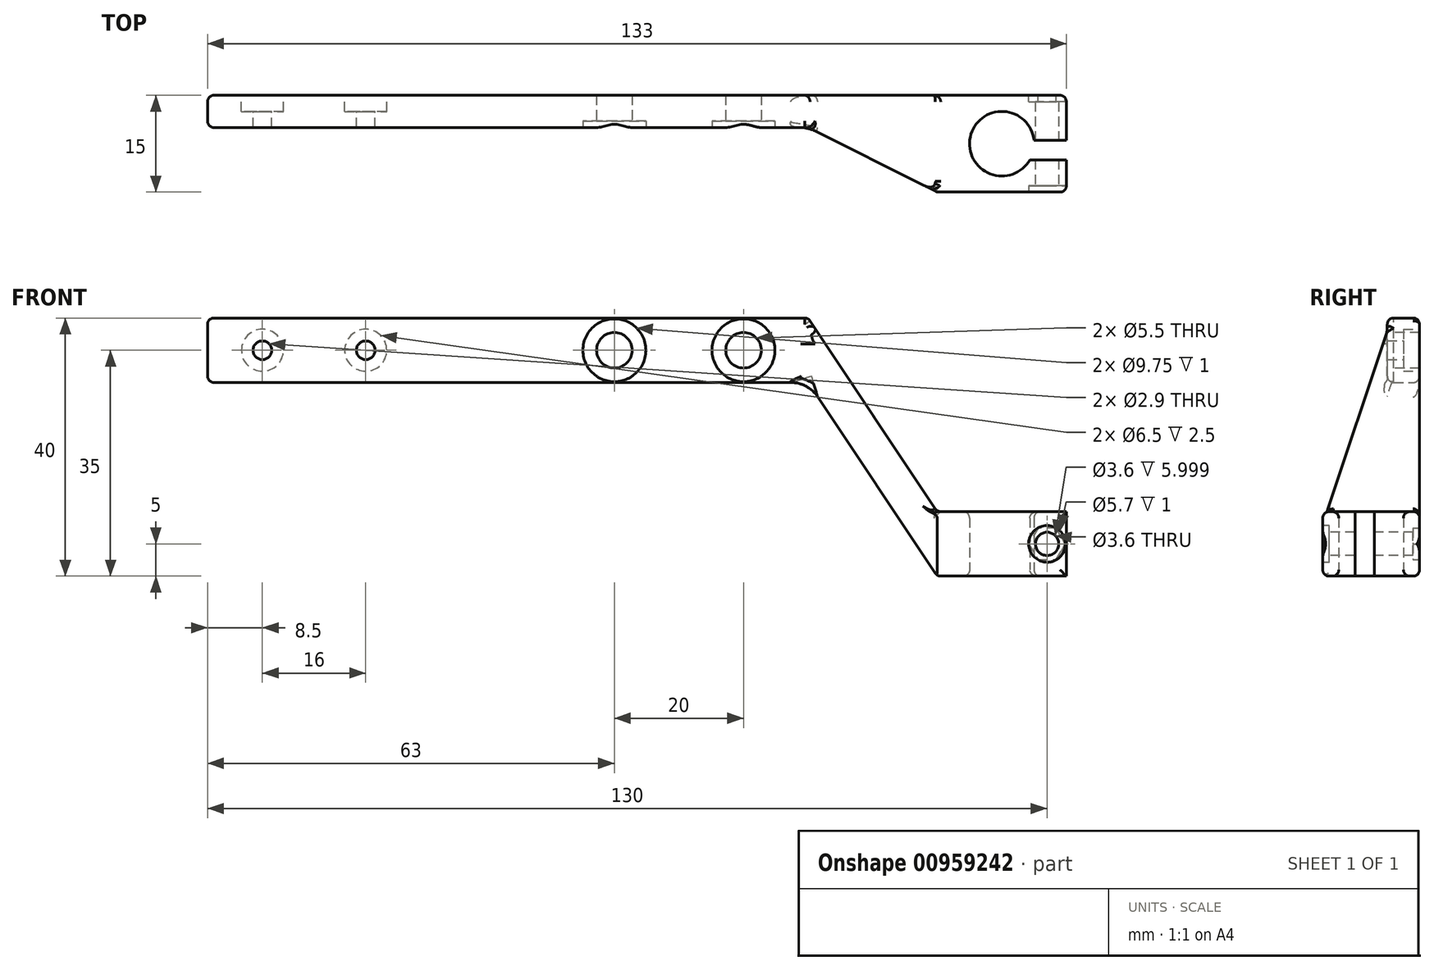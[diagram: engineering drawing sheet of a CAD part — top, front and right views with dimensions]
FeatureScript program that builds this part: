
annotation { "Feature Type Name" : "Feature", "Feature Type Description" : "" }
export const myFeature = defineFeature(function(context is Context, id is Id, definition is map)
    precondition{}
    {
        {
            var Q0;
            Q0=qCreatedBy(makeId("Top.planeOp"),FACE);
            var sketch = newSketch(context, id + "F0", { "sketchPlane" : qUnion([Q0])});
            skLineSegment(sketch, "E0.bottom", {"start": v(0, 0) * mm, "end": v(40, 0) * mm});
            skLineSegment(sketch, "E0.top", {"start": v(0, -5) * mm, "end": v(40, -5) * mm});
            skLineSegment(sketch, "E0.left", {"start": v(0, 0) * mm, "end": v(0, -5) * mm});
            skLineSegment(sketch, "E0.right", {"start": v(40, 0) * mm, "end": v(40, -5) * mm});
            skLineSegment(sketch, "E1.MirrorCS", {"start": v(80, 0) * mm, "end": v(40, 0) * mm});
            skLineSegment(sketch, "E2.MirrorCS", {"start": v(80, -5) * mm, "end": v(40, -5) * mm});
            skLineSegment(sketch, "E3.MirrorCS", {"start": v(80, 0) * mm, "end": v(80, -5) * mm});
            skPoint(sketch, "E4.oppositeSnap0", {"position": v(60, 0) * mm});
            skLineSegment(sketch, "E4.bottom", {"start": v(80, 0) * mm, "end": v(60, 0) * mm});
            skLineSegment(sketch, "E4.top", {"start": v(80, 5) * mm, "end": v(60, 5) * mm});
            skLineSegment(sketch, "E4.left", {"start": v(80, 0) * mm, "end": v(80, 5) * mm});
            skLineSegment(sketch, "E4.right", {"start": v(60, 0) * mm, "end": v(60, 5) * mm});
            skPoint(sketch, "E5.oppositeSnap0", {"position": v(60, -5) * mm});
            skLineSegment(sketch, "E5.bottom", {"start": v(80, -5) * mm, "end": v(60, -5) * mm});
            skLineSegment(sketch, "E5.top", {"start": v(80, -10) * mm, "end": v(60, -10) * mm});
            skLineSegment(sketch, "E5.left", {"start": v(80, -5) * mm, "end": v(80, -10) * mm});
            skLineSegment(sketch, "E5.right", {"start": v(60, -5) * mm, "end": v(60, -10) * mm});
            skLineSegment(sketch, "E6", {"start": v(40, -5) * mm, "end": v(60, -10) * mm});
            skLineSegment(sketch, "E7", {"start": v(40, 0) * mm, "end": v(60, 5) * mm});
            skPoint(sketch, "E8", {"position": v(70, -2.5) * mm});
            skPoint(sketch, "E8.positionSnap0", {"position": v(70, 0) * mm});
            skLineSegment(sketch, "E9", {"start": v(70, 0) * mm, "end": v(70, -5) * mm, "construction": true});
            skCircle(sketch, "E10", {"center": v(70, -2.5) * mm, "radius": 5 * mm});
            skLineSegment(sketch, "E11.bottom", {"start": v(80, -3) * mm, "end": v(74.97, -3) * mm});
            skLineSegment(sketch, "E11.top", {"start": v(80, -3) * mm, "end": v(74.97, -3) * mm});
            skLineSegment(sketch, "E11.left", {"start": v(80, -3) * mm, "end": v(80, -3) * mm});
            skLineSegment(sketch, "E11.right", {"start": v(74.97, -3) * mm, "end": v(74.97, -3) * mm});
            skLineSegment(sketch, "E12", {"start": v(70, -2.5) * mm, "end": v(80, -2.5) * mm, "construction": true});
            skLineSegment(sketch, "E13.MirrorCS", {"start": v(80, -2) * mm, "end": v(74.97, -2) * mm});
            skLineSegment(sketch, "E14", {"start": v(60, 0) * mm, "end": v(60, -5) * mm});
            skSolve(sketch);
        }
        {
            var Q0;
            Q0=makeQuery(id+"F0.imprint","IMPRINT",FACE,{"disambiguationData":[TD([[makeQuery(id+"F0.imprint","IMPRINT",EDGE,{"derivedFrom":sQuery(id+"F0.wireOp",EDGE,"E0.bottom")}),-1.0]])]});
            extrude(context, id + "F1", {"entities" : qUnion([Q0]), "depth" : 10 * mm, "offsetDistance" : 25 * mm});
        }
        {
            var Q0;
            Q0=makeQuery(id+"F0.imprint","IMPRINT",FACE,{"disambiguationData":[TD([[makeQuery(id+"F0.imprint","IMPRINT",EDGE,{"derivedFrom":sQuery(id+"F0.wireOp",EDGE,"E5.top")}),-1.0]])]});
            var Q1;
            {var subQ0=sQuery(id+"F0.wireOp",EDGE,"E14");Q1=makeQuery(id+"F0.imprint","IMPRINT",FACE,{"disambiguationData":[TD([[makeQuery(id+"F0.imprint","IMPRINT",EDGE,{"derivedFrom":subQ0}),1.0]])]});}
            var Q2;
            Q2=makeQuery(id+"F0.imprint","IMPRINT",FACE,{"disambiguationData":[TD([[makeQuery(id+"F0.imprint","IMPRINT",EDGE,{"derivedFrom":sQuery(id+"F0.wireOp",EDGE,"E4.top")}),1.0]])]});
            var Q3;
            {var subQ3=sQuery(id+"F0.wireOp",EDGE,"E13.MirrorCS");Q3=makeQuery(id+"F0.imprint","IMPRINT",FACE,{"disambiguationData":[TD([[makeQuery(id+"F0.imprint","IMPRINT",EDGE,{"derivedFrom":subQ3}),-1.0]])]});}
            var Q4;
            {var subQ3=sQuery(id+"F0.wireOp",EDGE,"E11.top");Q4=makeQuery(id+"F0.imprint","IMPRINT",FACE,{"disambiguationData":[TD([[makeQuery(id+"F0.imprint","IMPRINT",EDGE,{"derivedFrom":subQ3}),1.0]])]});}
            extrude(context, id + "F2", {"entities" : qUnion([Q0, Q1, Q2, Q3, Q4]), "operationType" : NewBodyOperationType.ADD, "depth" : 10 * mm, "offsetDistance" : 25 * mm});
        }
        {
            var Q0;
            Q0=makeQuery(id+"F1.opExtrude","SWEPT_FACE",FACE,{"disambiguationData":[OSD([sQuery(id+"F0.wireOp",EDGE,"E0.top")])]});
            var sketch = newSketch(context, id + "F3", { "sketchPlane" : qUnion([Q0])});
            skLineSegment(sketch, "E15", {"start": v(0, 5) * mm, "end": v(10, 5) * mm, "construction": true});
            skLineSegment(sketch, "E16", {"start": v(10, 5) * mm, "end": v(30, 5) * mm, "construction": true});
            skLineSegment(sketch, "E17", {"start": v(30, 5) * mm, "end": v(40, 5) * mm, "construction": true});
            skSolve(sketch);
        }
        {
            var Q0;
            Q0=makeQuery(id+"F2.opExtrude","SWEPT_FACE",FACE,{"disambiguationData":[OSD([sQuery(id+"F0.wireOp",EDGE,"E5.top")])]});
            var sketch = newSketch(context, id + "F4", { "sketchPlane" : qUnion([Q0])});
            skLineSegment(sketch, "E18", {"start": v(80, 5) * mm, "end": v(77, 5) * mm, "construction": true});
            skLineSegment(sketch, "E19", {"start": v(77, 5) * mm, "end": v(60, 5) * mm, "construction": true});
            skSolve(sketch);
        }
        {
            var Q0;
            Q0=sQuery(id+"F3.wireOp",VERTEX,"E15.end");
            var Q1;
            Q1=sQuery(id+"F3.wireOp",VERTEX,"E16.end");
            var Q2;
            Q2=makeQuery(id+"F1.opExtrude","SWEPT_BODY",BODY,{"disambiguationData":[OSD([sQuery(id+"F0.wireOp",EDGE,"E0.bottom"),sQuery(id+"F0.wireOp",EDGE,"E0.top"),sQuery(id+"F0.wireOp",EDGE,"E0.left"),sQuery(id+"F0.wireOp",EDGE,"E3.MirrorCS"),sQuery(id+"F0.wireOp",EDGE,"E4.top"),sQuery(id+"F0.wireOp",EDGE,"E4.left"),sQuery(id+"F0.wireOp",EDGE,"E5.top"),sQuery(id+"F0.wireOp",EDGE,"E5.left"),sQuery(id+"F0.wireOp",EDGE,"E6"),sQuery(id+"F0.wireOp",EDGE,"E7"),sQuery(id+"F0.wireOp",EDGE,"E10"),sQuery(id+"F0.wireOp",EDGE,"E11.top"),sQuery(id+"F0.wireOp",EDGE,"E13.MirrorCS")])]});
            hole(context, id + "F5", {"style" : HoleStyle.C_BORE, "endStyle" : HoleEndStyle.THROUGH, "holeDiameter" : 5.5 * mm, "cBoreDiameter" : 9.75 * mm, "cBoreDepth" : 1 * mm, "majorDiameter" : 5 * mm, "isTappedThrough" : true, "tappedDepth" : 12 * mm, "tapClearance" : 3, "locations" : qUnion([Q0, Q1]), "scope" : qUnion([Q2])});
        }
        {
            var Q0;
            Q0=sQuery(id+"F4.wireOp",VERTEX,"E18.end");
            var Q1;
            Q1=makeQuery(id+"F2.opExtrude","SWEPT_BODY",BODY,{"disambiguationData":[OSD([sQuery(id+"F0.wireOp",EDGE,"E3.MirrorCS"),sQuery(id+"F0.wireOp",EDGE,"E4.top"),sQuery(id+"F0.wireOp",EDGE,"E4.left"),sQuery(id+"F0.wireOp",EDGE,"E4.right"),sQuery(id+"F0.wireOp",EDGE,"E5.top"),sQuery(id+"F0.wireOp",EDGE,"E5.left"),sQuery(id+"F0.wireOp",EDGE,"E5.right"),sQuery(id+"F0.wireOp",EDGE,"E10"),sQuery(id+"F0.wireOp",EDGE,"E11.top"),sQuery(id+"F0.wireOp",EDGE,"E13.MirrorCS"),sQuery(id+"F0.wireOp",EDGE,"E14")])]});
            hole(context, id + "F6", {"style" : HoleStyle.C_BORE, "endStyle" : HoleEndStyle.THROUGH, "holeDiameter" : 3.6 * mm, "cBoreDiameter" : 5.7 * mm, "cBoreDepth" : 1 * mm, "majorDiameter" : 5 * mm, "isTappedThrough" : true, "tappedDepth" : 12 * mm, "tapClearance" : 3, "locations" : qUnion([Q0]), "scope" : qUnion([Q1])});
        }
        {
            var Q0;
            Q0=makeQuery(id+"F2.opExtrude","SWEPT_FACE",FACE,{"disambiguationData":[OSD([sQuery(id+"F0.wireOp",EDGE,"E4.top")])]});
            var sketch = newSketch(context, id + "F7", { "sketchPlane" : qUnion([Q0])});
            skCircle(sketch, "E20.cCircle", {"center": v(-77, 5) * mm, "radius": 2.45 * mm, "construction": true});
            skLineSegment(sketch, "E20.0", {"start": v(-75.58, 2.55) * mm, "end": v(-78.42, 2.55) * mm});
            skLineSegment(sketch, "E20.1", {"start": v(-78.42, 2.55) * mm, "end": v(-79.83, 5) * mm});
            skLineSegment(sketch, "E20.2", {"start": v(-79.83, 5) * mm, "end": v(-78.42, 7.45) * mm});
            skLineSegment(sketch, "E20.3", {"start": v(-78.42, 7.45) * mm, "end": v(-75.58, 7.45) * mm});
            skLineSegment(sketch, "E20.4", {"start": v(-75.58, 7.45) * mm, "end": v(-74.17, 5) * mm});
            skLineSegment(sketch, "E20.5", {"start": v(-74.17, 5) * mm, "end": v(-75.58, 2.55) * mm});
            skPoint(sketch, "E20.0.midPoint", {"position": v(-77, 2.55) * mm});
            skSolve(sketch);
        }
        {
            var Q0;
            Q0=makeQuery(id+"F7.imprint","IMPRINT",FACE,{"disambiguationData":[TD([[makeQuery(id+"F7.imprint","IMPRINT",EDGE,{"derivedFrom":makeQuery(id+"F6.hole-0.boolean.opBoolean","INTERSECT",EDGE,{"derivedFrom":[makeQuery(id+"F2.opExtrude","SWEPT_FACE",FACE,{"disambiguationData":[OSD([sQuery(id+"F0.wireOp",EDGE,"E4.top")])]}),makeQuery(id+"F6.hole-0.opRevolve","SWEPT_FACE",FACE,{"disambiguationData":[OSD([sQuery(id+"F6.hole-0.sketch.wireOp",EDGE,"core_line_2")])]})]})}),1.0]])]});
            var Q1;
            Q1=makeQuery(id+"F7.imprint","IMPRINT",FACE,{"disambiguationData":[TD([[makeQuery(id+"F7.imprint","IMPRINT",EDGE,{"derivedFrom":sQuery(id+"F7.wireOp",EDGE,"E20.0")}),-1.0]])]});
            extrude(context, id + "F8", {"entities" : qUnion([Q0, Q1]), "operationType" : NewBodyOperationType.REMOVE, "oppositeDirection" : true, "depth" : 1 * mm, "offsetDistance" : 25 * mm});
        }
        {
            var Q0;
            Q0=makeQuery(id+"F2.opExtrude","SWEPT_BODY",BODY,{"disambiguationData":[OSD([sQuery(id+"F0.wireOp",EDGE,"E3.MirrorCS"),sQuery(id+"F0.wireOp",EDGE,"E4.top"),sQuery(id+"F0.wireOp",EDGE,"E4.left"),sQuery(id+"F0.wireOp",EDGE,"E4.right"),sQuery(id+"F0.wireOp",EDGE,"E5.top"),sQuery(id+"F0.wireOp",EDGE,"E5.left"),sQuery(id+"F0.wireOp",EDGE,"E5.right"),sQuery(id+"F0.wireOp",EDGE,"E10"),sQuery(id+"F0.wireOp",EDGE,"E11.top"),sQuery(id+"F0.wireOp",EDGE,"E13.MirrorCS"),sQuery(id+"F0.wireOp",EDGE,"E14")])]});
            var Q1;
            Q1=makeQuery(id+"F1.opExtrude","SWEPT_EDGE",EDGE,{"disambiguationData":[OSD([sQuery(id+"F0.wireOp",EDGE,"E0.top"),sQuery(id+"F0.wireOp",EDGE,"E0.left")])]});
            transform(context, id + "F9", {"entities" : qUnion([Q0]), "transformType" : TransformType.TRANSLATION_DISTANCE, "transformDirection" : qUnion([Q1]), "distance" : 30 * mm, "makeCopy" : false});
        }
        {
            var Q0;
            Q0=makeQuery(id+"F2.opExtrude","SWEPT_BODY",BODY,{"disambiguationData":[OSD([sQuery(id+"F0.wireOp",EDGE,"E3.MirrorCS"),sQuery(id+"F0.wireOp",EDGE,"E4.top"),sQuery(id+"F0.wireOp",EDGE,"E4.left"),sQuery(id+"F0.wireOp",EDGE,"E4.right"),sQuery(id+"F0.wireOp",EDGE,"E5.top"),sQuery(id+"F0.wireOp",EDGE,"E5.left"),sQuery(id+"F0.wireOp",EDGE,"E5.right"),sQuery(id+"F0.wireOp",EDGE,"E10"),sQuery(id+"F0.wireOp",EDGE,"E11.top"),sQuery(id+"F0.wireOp",EDGE,"E13.MirrorCS"),sQuery(id+"F0.wireOp",EDGE,"E14")])]});
            var Q1;
            Q1=sQuery(id+"F0.wireOp",EDGE,"E5.right");
            transform(context, id + "F10", {"entities" : qUnion([Q0]), "transformType" : TransformType.TRANSLATION_ENTITY, "oppositeDirectionEntity" : false, "transformLine" : qUnion([Q1]), "makeCopy" : false});
        }
        {
            var Q0;
            Q0=makeQuery(id+"F1.opExtrude","SWEPT_FACE",FACE,{"disambiguationData":[OSD([sQuery(id+"F0.wireOp",EDGE,"E0.right")])]});
            var Q1;
            Q1=makeQuery(id+"F2.opExtrude","SWEPT_FACE",FACE,{"disambiguationData":[OSD([sQuery(id+"F0.wireOp",EDGE,"E4.right"),sQuery(id+"F0.wireOp",EDGE,"E5.right"),sQuery(id+"F0.wireOp",EDGE,"E14")])]});
            loft(context, id + "F11", {"operationType" : NewBodyOperationType.ADD, "sheetProfilesArray" : [{ "sheetProfileEntities" : qUnion([Q0]) }, { "sheetProfileEntities" : qUnion([Q1]) }]});
        }
        {
            var Q0;
            Q0=makeQuery(id+"F1.opExtrude","SWEPT_FACE",FACE,{"disambiguationData":[OSD([sQuery(id+"F0.wireOp",EDGE,"E0.left")])]});
            extrude(context, id + "F12", {"entities" : qUnion([Q0]), "operationType" : NewBodyOperationType.ADD, "depth" : 20 * mm, "offsetDistance" : 25 * mm});
        }
        {
            var Q0;
            Q0=makeQuery(id+"F12.opExtrude","CAP_FACE",FACE,{"disambiguationData":[OSD([sQuery(id+"F0.wireOp",EDGE,"E0.left")])],"isStart":false});
            extrude(context, id + "F13", {"entities" : qUnion([Q0]), "operationType" : NewBodyOperationType.ADD, "depth" : 33 * mm, "offsetDistance" : 25 * mm});
        }
        {
            var Q0;
            Q0=makeQuery(id+"F13.opExtrude","SWEPT_FACE",FACE,{"disambiguationData":[OSD([sQuery(id+"F0.wireOp",EDGE,"E0.top"),sQuery(id+"F0.wireOp",EDGE,"E0.left")])]});
            var sketch = newSketch(context, id + "F14", { "sketchPlane" : qUnion([Q0])});
            skLineSegment(sketch, "E21", {"start": v(-53, 5) * mm, "end": v(-44.5, 5) * mm, "construction": true});
            skPoint(sketch, "E22", {"position": v(-44.5, 5) * mm});
            skPoint(sketch, "E23", {"position": v(-28.5, 5) * mm});
            skLineSegment(sketch, "E24.trimOffspring", {"start": v(-28.5, 5) * mm, "end": v(-20, 5) * mm, "construction": true});
            skLineSegment(sketch, "E25", {"start": v(-44.5, 5) * mm, "end": v(-28.5, 5) * mm, "construction": true});
            skSolve(sketch);
        }
        {
            var Q0;
            {var subQ0=sQuery(id+"F0.wireOp",EDGE,"E0.left");var subQ1=sQuery(id+"F0.wireOp",EDGE,"E0.bottom");var subQ2=sQuery(id+"F0.wireOp",EDGE,"E4.top");Q0=makeQuery(id+"F13.boolean.opBoolean","MERGE",FACE,{"derivedFrom":[makeQuery(id+"F12.boolean.opBoolean","MERGE",FACE,{"derivedFrom":[makeQuery(id+"F11.boolean.opBoolean","MERGE",FACE,{"derivedFrom":[makeQuery(id+"F1.opExtrude","SWEPT_FACE",FACE,{"disambiguationData":[OSD([subQ1])]}),makeQuery(id+"F2.opExtrude","SWEPT_FACE",FACE,{"disambiguationData":[OSD([subQ2])]}),makeQuery(id+"F11.opLoft","SWEPT_FACE",FACE,{"disambiguationData":[OSD([subQ1,sQuery(id+"F0.wireOp",EDGE,"E0.right"),sQuery(id+"F0.wireOp",EDGE,"E1.MirrorCS"),subQ2,sQuery(id+"F0.wireOp",EDGE,"E4.right"),sQuery(id+"F0.wireOp",EDGE,"E7")])]})]}),makeQuery(id+"F12.opExtrude","SWEPT_FACE",FACE,{"disambiguationData":[OSD([subQ1,subQ0])]})]}),makeQuery(id+"F13.opExtrude","SWEPT_FACE",FACE,{"disambiguationData":[OSD([subQ1,subQ0])]})]});}
            var sketch = newSketch(context, id + "F15", { "sketchPlane" : qUnion([Q0])});
            skPoint(sketch, "E26.0", {"position": v(28.5, 5) * mm});
            skPoint(sketch, "E27.0", {"position": v(44.5, 5) * mm});
            skSolve(sketch);
        }
        {
            var Q0;
            Q0=sQuery(id+"F15.wireOp",VERTEX,"E26.0");
            var Q1;
            Q1=sQuery(id+"F15.wireOp",VERTEX,"E27.0");
            var Q2;
            Q2=makeQuery(id+"F1.opExtrude","SWEPT_BODY",BODY,{"disambiguationData":[OSD([sQuery(id+"F0.wireOp",EDGE,"E0.bottom"),sQuery(id+"F0.wireOp",EDGE,"E0.top"),sQuery(id+"F0.wireOp",EDGE,"E0.left"),sQuery(id+"F0.wireOp",EDGE,"E0.right")])]});
            hole(context, id + "F16", {"style" : HoleStyle.C_BORE, "endStyle" : HoleEndStyle.THROUGH, "holeDiameter" : 2.9 * mm, "cBoreDiameter" : 6.5 * mm, "cBoreDepth" : 2.5 * mm, "majorDiameter" : 5 * mm, "isTappedThrough" : true, "tappedDepth" : 12 * mm, "tapClearance" : 3, "locations" : qUnion([Q0, Q1]), "scope" : qUnion([Q2])});
        }
        {
            var Q0;
            {var subQ0=sQuery(id+"F0.wireOp",EDGE,"E6");var subQ1=sQuery(id+"F0.wireOp",EDGE,"E5.right");var subQ2=sQuery(id+"F0.wireOp",EDGE,"E5.top");var subQ3=sQuery(id+"F0.wireOp",EDGE,"E2.MirrorCS");var subQ4=sQuery(id+"F0.wireOp",EDGE,"E0.right");var subQ5=sQuery(id+"F0.wireOp",EDGE,"E0.top");Q0=makeQuery(id+"F11.opLoft","SWEPT_EDGE",EDGE,{"disambiguationData":[OSD([subQ5,subQ4,subQ3,subQ2,subQ1,subQ0]),TDD([makeQuery(id+"F1.opExtrude","CAP_VERTEX",VERTEX,{"disambiguationData":[OSD([subQ5,subQ4,subQ3,subQ0])],"isStart":false}),makeQuery(id+"F2.opExtrude","CAP_VERTEX",VERTEX,{"disambiguationData":[OSD([subQ2,subQ1,subQ0])],"isStart":false})])]});}
            fillet(context, id + "F17", {"entities" : qUnion([Q0]), "radius" : 1 * mm, "tangentPropagation" : true, "allowEdgeOverflow" : false});
        }
        {
            var Q0;
            {var subQ0=sQuery(id+"F0.wireOp",EDGE,"E0.left");var subQ1=sQuery(id+"F0.wireOp",EDGE,"E0.top");var subQ2=makeQuery(id+"F1.opExtrude","CAP_VERTEX",VERTEX,{"disambiguationData":[OSD([subQ1,subQ0])],"isStart":false});Q0=makeQuery(id+"F13.boolean.opBoolean","MERGE",EDGE,{"derivedFrom":[makeQuery(id+"F12.boolean.opBoolean","MERGE",EDGE,{"derivedFrom":[makeQuery(id+"F1.opExtrude","CAP_EDGE",EDGE,{"disambiguationData":[OSD([subQ1])],"isStart":false}),makeQuery(id+"F12.opExtrude","SWEPT_EDGE",EDGE,{"disambiguationData":[OSD([subQ1,subQ0]),TDD([subQ2])]})]}),makeQuery(id+"F13.opExtrude","SWEPT_EDGE",EDGE,{"disambiguationData":[OSD([subQ1,subQ0]),TDD([makeQuery(id+"F12.opExtrude","CAP_VERTEX",VERTEX,{"disambiguationData":[OSD([subQ1,subQ0]),TDD([subQ2])],"isStart":false})])]})]});}
            var Q1;
            Q1=makeQuery(id+"F13.opExtrude","CAP_EDGE",EDGE,{"disambiguationData":[OSD([sQuery(id+"F0.wireOp",EDGE,"E0.top"),sQuery(id+"F0.wireOp",EDGE,"E0.left")])],"isStart":false});
            var Q2;
            Q2=makeQuery(id+"F16.hole-0.boolean.opBoolean","COPY",EDGE,{"derivedFrom":makeQuery(id+"F16.hole-0.opRevolve","SWEPT_EDGE",EDGE,{"disambiguationData":[OSD([sQuery(id+"F16.hole-0.sketch.wireOp",EDGE,"cbore_start_line_2"),sQuery(id+"F16.hole-0.sketch.wireOp",EDGE,"cbore_start_line_3")])]})});
            var Q3;
            Q3=makeQuery(id+"F16.hole-1.boolean.opBoolean","COPY",EDGE,{"derivedFrom":makeQuery(id+"F16.hole-1.opRevolve","SWEPT_EDGE",EDGE,{"disambiguationData":[OSD([sQuery(id+"F16.hole-1.sketch.wireOp",EDGE,"cbore_start_line_2"),sQuery(id+"F16.hole-1.sketch.wireOp",EDGE,"cbore_start_line_3")])]})});
            var Q4;
            Q4=makeQuery(id+"F16.hole-0.boolean.opBoolean","COPY",EDGE,{"derivedFrom":makeQuery(id+"F16.hole-0.opRevolve","SWEPT_EDGE",EDGE,{"disambiguationData":[OSD([sQuery(id+"F16.hole-0.sketch.wireOp",EDGE,"cbore_start_line_1"),sQuery(id+"F16.hole-0.sketch.wireOp",EDGE,"core_line_2")])]})});
            var Q5;
            Q5=makeQuery(id+"F16.hole-1.boolean.opBoolean","COPY",EDGE,{"derivedFrom":makeQuery(id+"F16.hole-1.opRevolve","SWEPT_EDGE",EDGE,{"disambiguationData":[OSD([sQuery(id+"F16.hole-1.sketch.wireOp",EDGE,"cbore_start_line_1"),sQuery(id+"F16.hole-1.sketch.wireOp",EDGE,"core_line_2")])]})});
            var Q6;
            Q6=makeQuery(id+"F5.hole-0.boolean.opBoolean","COPY",EDGE,{"derivedFrom":makeQuery(id+"F5.hole-0.opRevolve","SWEPT_EDGE",EDGE,{"disambiguationData":[OSD([sQuery(id+"F5.hole-0.sketch.wireOp",EDGE,"cbore_start_line_2"),sQuery(id+"F5.hole-0.sketch.wireOp",EDGE,"cbore_start_line_3")])]})});
            var Q7;
            Q7=makeQuery(id+"F5.hole-0.boolean.opBoolean","COPY",EDGE,{"derivedFrom":makeQuery(id+"F5.hole-0.opRevolve","SWEPT_EDGE",EDGE,{"disambiguationData":[OSD([sQuery(id+"F5.hole-0.sketch.wireOp",EDGE,"cbore_start_line_1"),sQuery(id+"F5.hole-0.sketch.wireOp",EDGE,"core_line_2")])]})});
            var Q8;
            Q8=makeQuery(id+"F5.hole-1.boolean.opBoolean","COPY",EDGE,{"derivedFrom":makeQuery(id+"F5.hole-1.opRevolve","SWEPT_EDGE",EDGE,{"disambiguationData":[OSD([sQuery(id+"F5.hole-1.sketch.wireOp",EDGE,"cbore_start_line_1"),sQuery(id+"F5.hole-1.sketch.wireOp",EDGE,"core_line_2")])]})});
            var Q9;
            Q9=makeQuery(id+"F5.hole-1.boolean.opBoolean","COPY",EDGE,{"derivedFrom":makeQuery(id+"F5.hole-1.opRevolve","SWEPT_EDGE",EDGE,{"disambiguationData":[OSD([sQuery(id+"F5.hole-1.sketch.wireOp",EDGE,"cbore_start_line_2"),sQuery(id+"F5.hole-1.sketch.wireOp",EDGE,"cbore_start_line_3")])]})});
            var Q10;
            Q10=makeQuery(id+"F2.opExtrude","CAP_EDGE",EDGE,{"disambiguationData":[OSD([sQuery(id+"F0.wireOp",EDGE,"E5.top")])],"isStart":true});
            var Q11;
            Q11=makeQuery(id+"F2.opExtrude","CAP_EDGE",EDGE,{"disambiguationData":[OSD([sQuery(id+"F0.wireOp",EDGE,"E5.top")])],"isStart":false});
            var Q12;
            Q12=makeQuery(id+"F2.opExtrude","SWEPT_EDGE",EDGE,{"disambiguationData":[OSD([sQuery(id+"F0.wireOp",EDGE,"E5.top"),sQuery(id+"F0.wireOp",EDGE,"E5.left")])]});
            var Q13;
            Q13=makeQuery(id+"F2.opExtrude","SWEPT_EDGE",EDGE,{"disambiguationData":[OSD([sQuery(id+"F0.wireOp",EDGE,"E4.top"),sQuery(id+"F0.wireOp",EDGE,"E4.left")])]});
            var Q14;
            Q14=makeQuery(id+"F2.opExtrude","CAP_EDGE",EDGE,{"disambiguationData":[OSD([sQuery(id+"F0.wireOp",EDGE,"E4.top")])],"isStart":false});
            var Q15;
            {var subQ0=sQuery(id+"F0.wireOp",EDGE,"E14");var subQ1=sQuery(id+"F0.wireOp",EDGE,"E5.right");var subQ2=sQuery(id+"F0.wireOp",EDGE,"E4.right");var subQ3=makeQuery(id+"F2.opExtrude","CAP_EDGE",EDGE,{"disambiguationData":[OSD([subQ2,subQ1,subQ0])],"isStart":true});var subQ4=sQuery(id+"F0.wireOp",EDGE,"E6");var subQ5=sQuery(id+"F0.wireOp",EDGE,"E5.top");var subQ6=sQuery(id+"F0.wireOp",EDGE,"E7");var subQ7=sQuery(id+"F0.wireOp",EDGE,"E4.top");Q15=makeQuery(id+"F11.boolean.opBoolean","MERGE",EDGE,{"derivedFrom":[subQ3,makeQuery(id+"F11.opLoft","MID_CAP_EDGE",EDGE,{"disambiguationData":[OSD([subQ7,subQ2,subQ5,subQ1,subQ4,subQ6,subQ0]),TDD([makeQuery(id+"F2.opExtrude","CAP_VERTEX",VERTEX,{"disambiguationData":[OSD([subQ7,subQ2,subQ6])],"isStart":true}),makeQuery(id+"F2.opExtrude","CAP_VERTEX",VERTEX,{"disambiguationData":[OSD([subQ5,subQ1,subQ4])],"isStart":true}),subQ3])],"capPos":1.0})]});}
            var Q16;
            {var subQ0=sQuery(id+"F0.wireOp",EDGE,"E7");var subQ1=sQuery(id+"F0.wireOp",EDGE,"E4.right");var subQ2=sQuery(id+"F0.wireOp",EDGE,"E4.top");var subQ3=sQuery(id+"F0.wireOp",EDGE,"E1.MirrorCS");var subQ4=sQuery(id+"F0.wireOp",EDGE,"E0.right");var subQ5=sQuery(id+"F0.wireOp",EDGE,"E0.bottom");Q16=makeQuery(id+"F11.opLoft","SWEPT_EDGE",EDGE,{"disambiguationData":[OSD([subQ5,subQ4,subQ3,subQ2,subQ1,subQ0]),TDD([makeQuery(id+"F1.opExtrude","CAP_VERTEX",VERTEX,{"disambiguationData":[OSD([subQ5,subQ4,subQ3,subQ0])],"isStart":false}),makeQuery(id+"F2.opExtrude","CAP_VERTEX",VERTEX,{"disambiguationData":[OSD([subQ2,subQ1,subQ0])],"isStart":false})])]});}
            var Q17;
            {var subQ0=sQuery(id+"F0.wireOp",EDGE,"E7");var subQ1=sQuery(id+"F0.wireOp",EDGE,"E4.right");var subQ2=sQuery(id+"F0.wireOp",EDGE,"E4.top");var subQ3=sQuery(id+"F0.wireOp",EDGE,"E1.MirrorCS");var subQ4=sQuery(id+"F0.wireOp",EDGE,"E0.right");var subQ5=sQuery(id+"F0.wireOp",EDGE,"E0.bottom");Q17=makeQuery(id+"F11.opLoft","SWEPT_EDGE",EDGE,{"disambiguationData":[OSD([subQ5,subQ4,subQ3,subQ2,subQ1,subQ0]),TDD([makeQuery(id+"F1.opExtrude","CAP_VERTEX",VERTEX,{"disambiguationData":[OSD([subQ5,subQ4,subQ3,subQ0])],"isStart":true}),makeQuery(id+"F2.opExtrude","CAP_VERTEX",VERTEX,{"disambiguationData":[OSD([subQ2,subQ1,subQ0])],"isStart":true})])]});}
            var Q18;
            {var subQ0=sQuery(id+"F0.wireOp",EDGE,"E0.left");var subQ1=sQuery(id+"F0.wireOp",EDGE,"E0.bottom");var subQ2=makeQuery(id+"F1.opExtrude","CAP_VERTEX",VERTEX,{"disambiguationData":[OSD([subQ1,subQ0])],"isStart":false});Q18=makeQuery(id+"F13.boolean.opBoolean","MERGE",EDGE,{"derivedFrom":[makeQuery(id+"F12.boolean.opBoolean","MERGE",EDGE,{"derivedFrom":[makeQuery(id+"F1.opExtrude","CAP_EDGE",EDGE,{"disambiguationData":[OSD([subQ1])],"isStart":false}),makeQuery(id+"F12.opExtrude","SWEPT_EDGE",EDGE,{"disambiguationData":[OSD([subQ1,subQ0]),TDD([subQ2])]})]}),makeQuery(id+"F13.opExtrude","SWEPT_EDGE",EDGE,{"disambiguationData":[OSD([subQ1,subQ0]),TDD([makeQuery(id+"F12.opExtrude","CAP_VERTEX",VERTEX,{"disambiguationData":[OSD([subQ1,subQ0]),TDD([subQ2])],"isStart":false})])]})]});}
            var Q19;
            {var subQ0=sQuery(id+"F0.wireOp",EDGE,"E0.left");var subQ1=sQuery(id+"F0.wireOp",EDGE,"E0.bottom");var subQ2=makeQuery(id+"F1.opExtrude","CAP_VERTEX",VERTEX,{"disambiguationData":[OSD([subQ1,subQ0])],"isStart":true});Q19=makeQuery(id+"F13.boolean.opBoolean","MERGE",EDGE,{"derivedFrom":[makeQuery(id+"F12.boolean.opBoolean","MERGE",EDGE,{"derivedFrom":[makeQuery(id+"F1.opExtrude","CAP_EDGE",EDGE,{"disambiguationData":[OSD([subQ1])],"isStart":true}),makeQuery(id+"F12.opExtrude","SWEPT_EDGE",EDGE,{"disambiguationData":[OSD([subQ1,subQ0]),TDD([subQ2])]})]}),makeQuery(id+"F13.opExtrude","SWEPT_EDGE",EDGE,{"disambiguationData":[OSD([subQ1,subQ0]),TDD([makeQuery(id+"F12.opExtrude","CAP_VERTEX",VERTEX,{"disambiguationData":[OSD([subQ1,subQ0]),TDD([subQ2])],"isStart":false})])]})]});}
            var Q20;
            Q20=makeQuery(id+"F2.opExtrude","CAP_EDGE",EDGE,{"disambiguationData":[OSD([sQuery(id+"F0.wireOp",EDGE,"E4.top")])],"isStart":true});
            var Q21;
            Q21=makeQuery(id+"F13.opExtrude","CAP_EDGE",EDGE,{"disambiguationData":[OSD([sQuery(id+"F0.wireOp",EDGE,"E0.bottom"),sQuery(id+"F0.wireOp",EDGE,"E0.left")])],"isStart":false});
            var Q22;
            {var subQ0=sQuery(id+"F0.wireOp",EDGE,"E0.left");var subQ1=sQuery(id+"F0.wireOp",EDGE,"E0.top");var subQ2=makeQuery(id+"F1.opExtrude","CAP_VERTEX",VERTEX,{"disambiguationData":[OSD([subQ1,subQ0])],"isStart":true});Q22=makeQuery(id+"F13.boolean.opBoolean","MERGE",EDGE,{"derivedFrom":[makeQuery(id+"F12.boolean.opBoolean","MERGE",EDGE,{"derivedFrom":[makeQuery(id+"F1.opExtrude","CAP_EDGE",EDGE,{"disambiguationData":[OSD([subQ1])],"isStart":true}),makeQuery(id+"F12.opExtrude","SWEPT_EDGE",EDGE,{"disambiguationData":[OSD([subQ1,subQ0]),TDD([subQ2])]})]}),makeQuery(id+"F13.opExtrude","SWEPT_EDGE",EDGE,{"disambiguationData":[OSD([subQ1,subQ0]),TDD([makeQuery(id+"F12.opExtrude","CAP_VERTEX",VERTEX,{"disambiguationData":[OSD([subQ1,subQ0]),TDD([subQ2])],"isStart":false})])]})]});}
            var Q23;
            {var subQ0=sQuery(id+"F0.wireOp",EDGE,"E0.left");Q23=makeQuery(id+"F13.opExtrude","CAP_EDGE",EDGE,{"disambiguationData":[OSD([subQ0]),TDD([makeQuery(id+"F12.opExtrude","CAP_EDGE",EDGE,{"disambiguationData":[OSD([subQ0]),TDD([makeQuery(id+"F1.opExtrude","CAP_EDGE",EDGE,{"disambiguationData":[OSD([subQ0])],"isStart":false})])],"isStart":false})])],"isStart":false});}
            var Q24;
            {var subQ0=sQuery(id+"F0.wireOp",EDGE,"E0.left");Q24=makeQuery(id+"F13.opExtrude","CAP_EDGE",EDGE,{"disambiguationData":[OSD([subQ0]),TDD([makeQuery(id+"F12.opExtrude","CAP_EDGE",EDGE,{"disambiguationData":[OSD([subQ0]),TDD([makeQuery(id+"F1.opExtrude","CAP_EDGE",EDGE,{"disambiguationData":[OSD([subQ0])],"isStart":true})])],"isStart":false})])],"isStart":false});}
            var Q25;
            Q25=makeQuery(id+"F2.opExtrude","CAP_EDGE",EDGE,{"disambiguationData":[OSD([sQuery(id+"F0.wireOp",EDGE,"E10")])],"isStart":false});
            var Q26;
            Q26=makeQuery(id+"F2.opExtrude","CAP_EDGE",EDGE,{"disambiguationData":[OSD([sQuery(id+"F0.wireOp",EDGE,"E10")])],"isStart":true});
            var Q27;
            Q27=makeQuery(id+"F6.hole-0.boolean.opBoolean","COPY",EDGE,{"derivedFrom":makeQuery(id+"F6.hole-0.opRevolve","SWEPT_EDGE",EDGE,{"disambiguationData":[OSD([sQuery(id+"F6.hole-0.sketch.wireOp",EDGE,"cbore_start_line_2"),sQuery(id+"F6.hole-0.sketch.wireOp",EDGE,"cbore_start_line_3")])]})});
            fillet(context, id + "F18", {"entities" : qUnion([Q0, Q1, Q2, Q3, Q4, Q5, Q6, Q7, Q8, Q9, Q10, Q11, Q12, Q13, Q14, Q15, Q16, Q17, Q18, Q19, Q20, Q21, Q22, Q23, Q24, Q25, Q26, Q27]), "radius" : 1 * mm, "allowEdgeOverflow" : false});
        }
        {
            var Q0;
            {var subQ0=sQuery(id+"F0.wireOp",EDGE,"E6");var subQ1=sQuery(id+"F0.wireOp",EDGE,"E5.right");var subQ2=sQuery(id+"F0.wireOp",EDGE,"E5.top");var subQ3=sQuery(id+"F0.wireOp",EDGE,"E2.MirrorCS");var subQ4=sQuery(id+"F0.wireOp",EDGE,"E0.right");var subQ5=sQuery(id+"F0.wireOp",EDGE,"E0.top");Q0=makeQuery(id+"F11.opLoft","SWEPT_EDGE",EDGE,{"disambiguationData":[OSD([subQ5,subQ4,subQ3,subQ2,subQ1,subQ0]),TDD([makeQuery(id+"F1.opExtrude","CAP_VERTEX",VERTEX,{"disambiguationData":[OSD([subQ5,subQ4,subQ3,subQ0])],"isStart":true}),makeQuery(id+"F2.opExtrude","CAP_VERTEX",VERTEX,{"disambiguationData":[OSD([subQ2,subQ1,subQ0])],"isStart":true})])]});}
            var Q1;
            {var subQ0=sQuery(id+"F0.wireOp",EDGE,"E0.right");var subQ1=makeQuery(id+"F1.opExtrude","CAP_EDGE",EDGE,{"disambiguationData":[OSD([subQ0])],"isStart":false});var subQ2=sQuery(id+"F0.wireOp",EDGE,"E6");var subQ3=sQuery(id+"F0.wireOp",EDGE,"E2.MirrorCS");var subQ4=sQuery(id+"F0.wireOp",EDGE,"E0.top");var subQ5=sQuery(id+"F0.wireOp",EDGE,"E7");var subQ6=sQuery(id+"F0.wireOp",EDGE,"E1.MirrorCS");var subQ7=sQuery(id+"F0.wireOp",EDGE,"E0.bottom");Q1=makeQuery(id+"F11.boolean.opBoolean","MERGE",EDGE,{"derivedFrom":[subQ1,makeQuery(id+"F11.opLoft","MID_CAP_EDGE",EDGE,{"disambiguationData":[OSD([subQ7,subQ4,subQ0,subQ6,subQ3,subQ2,subQ5]),TDD([makeQuery(id+"F1.opExtrude","CAP_VERTEX",VERTEX,{"disambiguationData":[OSD([subQ7,subQ0,subQ6,subQ5])],"isStart":false}),makeQuery(id+"F1.opExtrude","CAP_VERTEX",VERTEX,{"disambiguationData":[OSD([subQ4,subQ0,subQ3,subQ2])],"isStart":false}),subQ1])],"capPos":0.0})]});}
            var Q2;
            {var subQ0=sQuery(id+"F0.wireOp",EDGE,"E14");var subQ1=sQuery(id+"F0.wireOp",EDGE,"E5.right");var subQ2=sQuery(id+"F0.wireOp",EDGE,"E4.right");var subQ3=makeQuery(id+"F2.opExtrude","CAP_EDGE",EDGE,{"disambiguationData":[OSD([subQ2,subQ1,subQ0])],"isStart":false});var subQ4=sQuery(id+"F0.wireOp",EDGE,"E6");var subQ5=sQuery(id+"F0.wireOp",EDGE,"E5.top");var subQ6=sQuery(id+"F0.wireOp",EDGE,"E7");var subQ7=sQuery(id+"F0.wireOp",EDGE,"E4.top");Q2=makeQuery(id+"F11.boolean.opBoolean","MERGE",EDGE,{"derivedFrom":[subQ3,makeQuery(id+"F11.opLoft","MID_CAP_EDGE",EDGE,{"disambiguationData":[OSD([subQ7,subQ2,subQ5,subQ1,subQ4,subQ6,subQ0]),TDD([makeQuery(id+"F2.opExtrude","CAP_VERTEX",VERTEX,{"disambiguationData":[OSD([subQ7,subQ2,subQ6])],"isStart":false}),makeQuery(id+"F2.opExtrude","CAP_VERTEX",VERTEX,{"disambiguationData":[OSD([subQ5,subQ1,subQ4])],"isStart":false}),subQ3])],"capPos":1.0})]});}
            fillet(context, id + "F19", {"entities" : qUnion([Q0, Q1, Q2]), "radius" : 1 * mm, "tangentPropagation" : true, "allowEdgeOverflow" : false});
        }
        {
            var Q0;
            {var subQ0=sQuery(id+"F0.wireOp",EDGE,"E6");var subQ1=sQuery(id+"F0.wireOp",EDGE,"E2.MirrorCS");var subQ2=sQuery(id+"F0.wireOp",EDGE,"E0.right");var subQ3=sQuery(id+"F0.wireOp",EDGE,"E0.top");Q0=makeQuery(id+"F11.boolean.opBoolean","MERGE",EDGE,{"derivedFrom":[makeQuery(id+"F1.opExtrude","SWEPT_EDGE",EDGE,{"disambiguationData":[OSD([subQ3,subQ2,subQ1,subQ0])]}),makeQuery(id+"F11.opLoft","MID_CAP_EDGE",EDGE,{"disambiguationData":[OSD([subQ3,subQ2,subQ1,subQ0])],"capPos":0.0})]});}
            fillet(context, id + "F20", {"entities" : qUnion([Q0]), "radius" : 5 * mm, "tangentPropagation" : true, "allowEdgeOverflow" : false});
        }
    });
